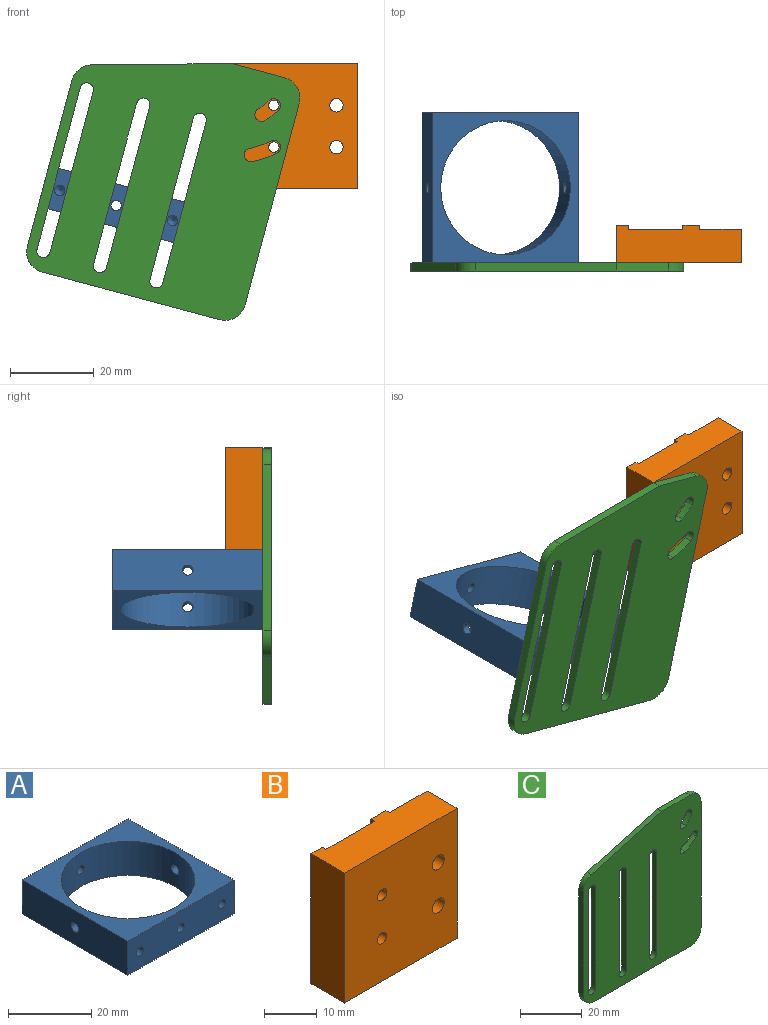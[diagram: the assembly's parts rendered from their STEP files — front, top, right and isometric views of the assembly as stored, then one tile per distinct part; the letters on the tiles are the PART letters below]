
ASSEMBLY  parts=3 mates=3
PART A: 15 faces, bbox 36x36x10 mm
  f0: cylinder r=16.05mm len=32.1mm, axis (0,0,1), area 988.8mm2, adj f5,f6,f7,f8,f9,f10
  f1: plane 36x10mm, normal (0,1,0), area 355.1mm2, adj f2,f4,f5,f6,f7
  f2: plane 36x10mm, normal (-1,0,0), area 355.1mm2, adj f1,f3,f5,f6,f10
  f3: plane 36x10mm, normal (0,-1,0), area 345.3mm2, adj f2,f4,f5,f6,f8,f12,f14
  f4: plane 36x10mm, normal (1,0,0), area 355.1mm2, adj f1,f3,f5,f6,f9
  f5: plane 36x36mm, normal (0,0,-1), area 486.7mm2, adj f0,f1,f2,f3,f4
  f6: plane 36x36mm, normal (0,0,1), area 486.7mm2, adj f0,f1,f2,f3,f4
  f7: cylinder r=1.25mm len=2.5mm, axis (0,1,0), area 15.5mm2, adj f0,f1
  f8: cylinder r=1.25mm len=2.5mm, axis (0,1,0), area 15.5mm2, adj f0,f3
  f9: cylinder r=1.25mm len=2.5mm, axis (-1,0,0), area 15.5mm2, adj f0,f4
  f10: cylinder r=1.25mm len=2.5mm, axis (-1,0,0), area 15.5mm2, adj f0,f2
  f11: cone r=0mm half-angle=59deg, axis (0,-1,0), area 5.7mm2, adj f12
  f12: cylinder r=1.25mm len=6mm, axis (0,-1,0), area 47.1mm2, adj f3,f11
  f13: cone r=0mm half-angle=59deg, axis (0,-1,0), area 5.7mm2, adj f14
  f14: cylinder r=1.25mm len=6mm, axis (0,-1,0), area 47.1mm2, adj f3,f13
PART B: 16 faces, bbox 30x9x30 mm
  f0: plane 30x1mm, normal (1,0,0), area 30mm2, adj f1,f9,f10,f11
  f1: plane 30x3mm, normal (0,1,0), area 90mm2, adj f0,f2,f10,f11
  f2: plane 30x9mm, normal (-1,0,0), area 270mm2, adj f1,f3,f10,f11
  f3: plane 30x30mm, normal (0,-1,0), area 874.1mm2, adj f2,f4,f10,f11,f12,f13,f14,f15
  f4: plane 30x8mm, normal (1,0,0), area 240mm2, adj f3,f5,f10,f11
  f5: plane 30x10mm, normal (0,1,0), area 283.9mm2, adj f4,f6,f10,f11,f12,f13
  f6: plane 30x1mm, normal (1,0,0), area 30mm2, adj f5,f7,f10,f11
  f7: plane 30x4mm, normal (0,1,0), area 120mm2, adj f6,f8,f10,f11
  f8: plane 30x1mm, normal (-1,0,0), area 30mm2, adj f7,f9,f10,f11
  f9: plane 30x13mm, normal (0,1,0), area 380.2mm2, adj f0,f8,f10,f11,f14,f15
  f10: plane 30x9mm, normal (0,0,-1), area 247mm2, adj f0,f1,f2,f3,f4,f5,f6,f7
  f11: plane 30x9mm, normal (0,0,1), area 247mm2, adj f0,f1,f2,f3,f4,f5,f6,f7
  f12: cylinder r=1.6mm len=8mm, axis (0,-1,0), area 80.4mm2, adj f3,f5
  f13: cylinder r=1.6mm len=8mm, axis (0,-1,0), area 80.4mm2, adj f3,f5
  f14: cylinder r=1.25mm len=8mm, axis (0,-1,0), area 62.8mm2, adj f3,f9
  f15: cylinder r=1.25mm len=8mm, axis (0,-1,0), area 62.8mm2, adj f3,f9
PART C: 31 faces, bbox 54x2x60 mm
  f0: plane 40x2mm, normal (1,0,0), area 80mm2, adj f1,f24,f25,f26
  f1: cylinder r=1.6mm len=3.2mm, axis (0,1,0), area 10.1mm2, adj f0,f2,f25,f26
  f2: plane 40x2mm, normal (-1,0,0), area 80mm2, adj f1,f24,f25,f26
  f3: cylinder r=1.6mm len=3.2mm, axis (0,1,0), area 10.1mm2, adj f4,f19,f25,f26
  f4: plane 40x2mm, normal (-1,0,0), area 80mm2, adj f3,f5,f25,f26
  f5: cylinder r=1.6mm len=3.2mm, axis (0,1,0), area 10.1mm2, adj f4,f19,f25,f26
  f6: plane 50x2mm, normal (1,0,0), area 100mm2, adj f25,f26,f27,f30
  f7: plane 13x2mm, normal (0,0,1), area 26mm2, adj f8,f25,f26,f27
  f8: plane 32.34x8.98mm, normal (-0.27,0,0.96), area 67.1mm2, adj f7,f25,f26,f28
  f9: plane 41.2x2mm, normal (-1,0,0), area 82.4mm2, adj f25,f26,f28,f29
  f10: plane 40x2mm, normal (1,0,0), area 80mm2, adj f11,f21,f25,f26
  f11: cylinder r=1.6mm len=3.2mm, axis (0,1,0), area 10.1mm2, adj f10,f12,f25,f26
  f12: plane 40x2mm, normal (-1,0,0), area 80mm2, adj f11,f21,f25,f26
  f13: cylinder r=1.6mm len=2.73mm, axis (0,1,0), area 10.1mm2, adj f14,f22,f25,f26
  f14: cylinder r=12.54mm len=2.6mm, axis (0,1,0), area 6.6mm2, adj f13,f15,f25,f26
  f15: cylinder r=1.6mm len=2.99mm, axis (0,1,0), area 10.1mm2, adj f14,f22,f25,f26
  f16: cylinder r=1.6mm len=3.03mm, axis (0,1,0), area 10.1mm2, adj f17,f23,f25,f26
  f17: cylinder r=20.76mm len=4.49mm, axis (0,1,0), area 10.9mm2, adj f16,f18,f25,f26
  f18: cylinder r=1.6mm len=2.8mm, axis (0,1,0), area 10.1mm2, adj f17,f23,f25,f26
  f19: plane 40x2mm, normal (1,0,0), area 80mm2, adj f3,f5,f25,f26
  f20: plane 44x2mm, normal (0,0,-1), area 88mm2, adj f25,f26,f29,f30
  f21: cylinder r=1.6mm len=3.2mm, axis (0,1,0), area 10.1mm2, adj f10,f12,f25,f26
  f22: cylinder r=15.74mm len=3.26mm, axis (0,1,0), area 8.2mm2, adj f13,f15,f25,f26
  f23: cylinder r=23.96mm len=5.18mm, axis (0,1,0), area 12.5mm2, adj f16,f18,f25,f26
  f24: cylinder r=1.6mm len=3.2mm, axis (0,1,0), area 10.1mm2, adj f0,f2,f25,f26
  f25: plane 60x54mm, normal (0,-1,0), area 2586.4mm2, adj f0,f1,f2,f3,f4,f5,f6,f7
  f26: plane 60x54mm, normal (0,1,0), area 2586.4mm2, adj f0,f1,f2,f3,f4,f5,f6,f7
  f27: cylinder r=5mm len=5mm, axis (0,1,0), area 15.7mm2, adj f6,f7,f25,f26
  f28: cylinder r=5mm len=4.82mm, axis (0,1,0), area 13mm2, adj f8,f9,f25,f26
  f29: cylinder r=5mm len=5mm, axis (0,1,0), area 15.7mm2, adj f9,f20,f25,f26
  f30: cylinder r=5mm len=5mm, axis (0,-1,0), area 15.7mm2, adj f6,f20,f25,f26
PLACE A rot(axis=(0,1,0),15deg) t=(-27.13,-2.34,-23.33)mm
PLACE B t=(-18.69,-2.34,5.82)mm
PLACE C rot(axis=(0,1,0),15deg) t=(-18.07,-2.34,10.48)mm
MATE parallel A.f11 <-> C.f5  axis (0,-1,0) through (-41.95,-20.34,-24.54)mm
MATE parallel B.f14 <-> C.f13  axis (0,-1,0) through (9.31,-20.34,-4.18)mm
MATE parallel A.f11 <-> C.f5  axis (0,-1,0) through (-41.95,-20.34,-24.54)mm
